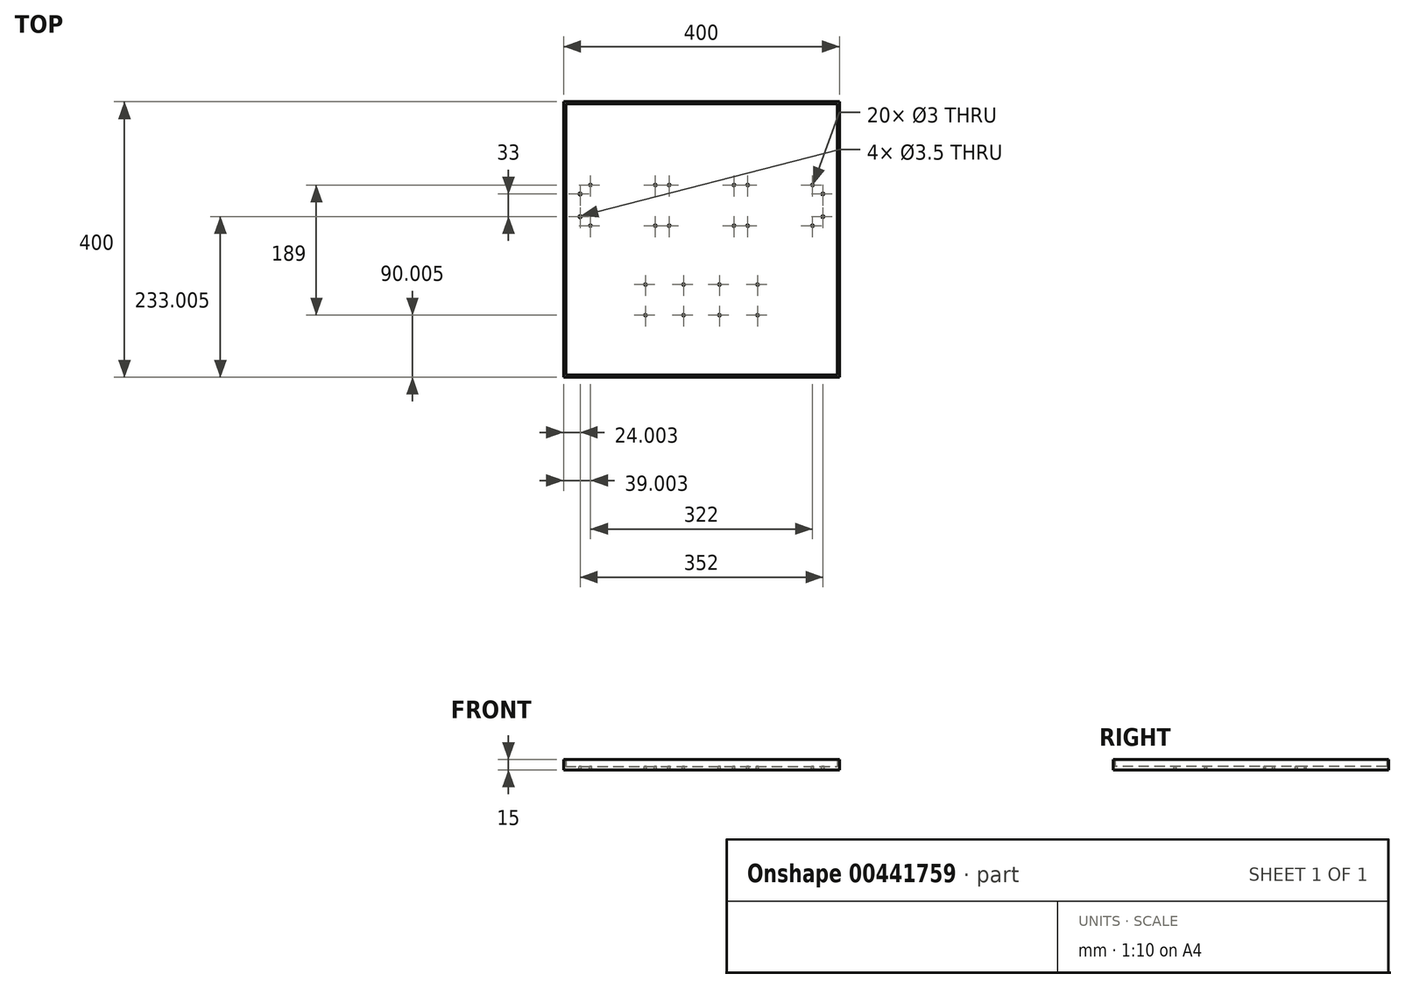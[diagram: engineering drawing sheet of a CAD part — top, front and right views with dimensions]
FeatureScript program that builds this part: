
annotation { "Feature Type Name" : "Feature", "Feature Type Description" : "" }
export const myFeature = defineFeature(function(context is Context, id is Id, definition is map)
    precondition{}
    {
        {
            var Q0;
            Q0=qCreatedBy(makeId("Top.planeOp"),FACE);
            var sketch = newSketch(context, id + "F0", { "sketchPlane" : qUnion([Q0])});
            skLineSegment(sketch, "E0.bottom", {"start": v(-197.38, 325.18) * mm, "end": v(202.62, 325.18) * mm});
            skLineSegment(sketch, "E0.top", {"start": v(-197.38, -74.82) * mm, "end": v(202.62, -74.82) * mm});
            skLineSegment(sketch, "E0.left", {"start": v(-197.38, 325.18) * mm, "end": v(-197.38, -74.82) * mm});
            skLineSegment(sketch, "E0.right", {"start": v(202.62, 325.18) * mm, "end": v(202.62, -74.82) * mm});
            skSolve(sketch);
        }
        {
            var Q0;
            Q0=qSketchRegion(id+"F0",true);
            extrude(context, id + "F1", {"entities" : qUnion([Q0]), "depth" : 5 * mm});
        }
        {
            var Q0;
            Q0=makeQuery(id+"F1.opExtrude","CAP_FACE",FACE,{"disambiguationData":[OSD([sQuery(id+"F0.wireOp",EDGE,"E0.bottom"),sQuery(id+"F0.wireOp",EDGE,"E0.top"),sQuery(id+"F0.wireOp",EDGE,"E0.left"),sQuery(id+"F0.wireOp",EDGE,"E0.right")])],"isStart":false});
            var sketch = newSketch(context, id + "F2", { "sketchPlane" : qUnion([Q0])});
            skCircle(sketch, "E1", {"center": v(-158.38, 145.18) * mm, "radius": 1.5 * mm});
            skCircle(sketch, "E2", {"center": v(-64.38, 145.18) * mm, "radius": 1.5 * mm});
            skCircle(sketch, "E3", {"center": v(-44.38, 145.18) * mm, "radius": 1.5 * mm});
            skCircle(sketch, "E4", {"center": v(49.62, 145.18) * mm, "radius": 1.5 * mm});
            skCircle(sketch, "E5", {"center": v(69.62, 145.18) * mm, "radius": 1.5 * mm});
            skCircle(sketch, "E6", {"center": v(163.62, 145.18) * mm, "radius": 1.5 * mm});
            skCircle(sketch, "E7.0.1.0", {"center": v(-44.38, 204.18) * mm, "radius": 1.5 * mm});
            skCircle(sketch, "E7.0.1.1", {"center": v(-158.38, 204.18) * mm, "radius": 1.5 * mm});
            skCircle(sketch, "E7.0.1.2", {"center": v(49.62, 204.18) * mm, "radius": 1.5 * mm});
            skCircle(sketch, "E7.0.1.3", {"center": v(69.62, 204.18) * mm, "radius": 1.5 * mm});
            skCircle(sketch, "E7.0.1.4", {"center": v(163.62, 204.18) * mm, "radius": 1.5 * mm});
            skCircle(sketch, "E7.0.1.5", {"center": v(-64.38, 204.18) * mm, "radius": 1.5 * mm});
            skLineSegment(sketch, "E7.direction1", {"start": v(-158.38, 145.18) * mm, "end": v(-133.38, 145.18) * mm, "construction": true});
            skLineSegment(sketch, "E7.direction2", {"start": v(-158.38, 145.18) * mm, "end": v(-158.38, 204.18) * mm, "construction": true});
            skCircle(sketch, "E8", {"center": v(-173.38, 158.18) * mm, "radius": 1.75 * mm});
            skCircle(sketch, "E9.0.1.0", {"center": v(-173.38, 191.18) * mm, "radius": 1.75 * mm});
            skLineSegment(sketch, "E9.direction1", {"start": v(-173.38, 158.18) * mm, "end": v(178.62, 158.18) * mm, "construction": true});
            skLineSegment(sketch, "E9.direction2", {"start": v(-173.38, 158.18) * mm, "end": v(-173.38, 191.18) * mm, "construction": true});
            skCircle(sketch, "E10.0.1.0", {"center": v(178.62, 158.18) * mm, "radius": 1.75 * mm});
            skCircle(sketch, "E10.0.1.1", {"center": v(178.62, 191.18) * mm, "radius": 1.75 * mm});
            skSolve(sketch);
        }
        {
            var Q0;
            Q0=qSketchRegion(id+"F2",true);
            extrude(context, id + "F3", {"entities" : qUnion([Q0]), "operationType" : NewBodyOperationType.REMOVE, "endBound" : BoundingType.THROUGH_ALL, "oppositeDirection" : true, "depth" : 25 * mm});
        }
        {
            var Q0;
            Q0=makeQuery(id+"F1.opExtrude","CAP_FACE",FACE,{"disambiguationData":[OSD([sQuery(id+"F0.wireOp",EDGE,"E0.bottom"),sQuery(id+"F0.wireOp",EDGE,"E0.top"),sQuery(id+"F0.wireOp",EDGE,"E0.left"),sQuery(id+"F0.wireOp",EDGE,"E0.right")])],"isStart":false});
            var sketch = newSketch(context, id + "F4", { "sketchPlane" : qUnion([Q0])});
            skCircle(sketch, "E11", {"center": v(-23.38, 15.18) * mm, "radius": 1.5 * mm});
            skCircle(sketch, "E12.0.1.0", {"center": v(-23.38, 59.63) * mm, "radius": 1.5 * mm});
            skCircle(sketch, "E12.1.0.0", {"center": v(28.62, 15.18) * mm, "radius": 1.5 * mm});
            skCircle(sketch, "E12.1.1.0", {"center": v(28.62, 59.63) * mm, "radius": 1.5 * mm});
            skLineSegment(sketch, "E12.direction1", {"start": v(-23.38, 15.18) * mm, "end": v(28.62, 15.18) * mm, "construction": true});
            skLineSegment(sketch, "E12.direction2", {"start": v(-23.38, 15.18) * mm, "end": v(-23.38, 59.63) * mm, "construction": true});
            skSolve(sketch);
        }
        {
            var Q0;
            Q0=qSketchRegion(id+"F4",true);
            extrude(context, id + "F5", {"entities" : qUnion([Q0]), "operationType" : NewBodyOperationType.REMOVE, "endBound" : BoundingType.THROUGH_ALL, "oppositeDirection" : true, "depth" : 25 * mm});
        }
        {
            var Q0;
            Q0=makeQuery(id+"F1.opExtrude","CAP_FACE",FACE,{"disambiguationData":[OSD([sQuery(id+"F0.wireOp",EDGE,"E0.bottom"),sQuery(id+"F0.wireOp",EDGE,"E0.top"),sQuery(id+"F0.wireOp",EDGE,"E0.left"),sQuery(id+"F0.wireOp",EDGE,"E0.right")])],"isStart":false});
            var sketch = newSketch(context, id + "F6", { "sketchPlane" : qUnion([Q0])});
            skCircle(sketch, "E13", {"center": v(-78.65, 15.18) * mm, "radius": 1.5 * mm});
            skCircle(sketch, "E14.0.1.0", {"center": v(-78.65, 59.63) * mm, "radius": 1.5 * mm});
            skCircle(sketch, "E14.1.0.0", {"center": v(83.9, 15.18) * mm, "radius": 1.5 * mm});
            skCircle(sketch, "E14.1.1.0", {"center": v(83.9, 59.63) * mm, "radius": 1.5 * mm});
            skLineSegment(sketch, "E14.direction1", {"start": v(-78.65, 15.18) * mm, "end": v(83.9, 15.18) * mm, "construction": true});
            skLineSegment(sketch, "E14.direction2", {"start": v(-78.65, 15.18) * mm, "end": v(-78.65, 59.63) * mm, "construction": true});
            skSolve(sketch);
        }
        {
            var Q0;
            Q0=qSketchRegion(id+"F6",true);
            extrude(context, id + "F7", {"entities" : qUnion([Q0]), "operationType" : NewBodyOperationType.REMOVE, "endBound" : BoundingType.THROUGH_ALL, "oppositeDirection" : true, "depth" : 25 * mm});
        }
        {
            assignVariable(context, id + "F8", {"name" : "H", "anyValue" : 10});
        }
        {
            var Q0;
            Q0=makeQuery(id+"F1.opExtrude","CAP_FACE",FACE,{"disambiguationData":[OSD([sQuery(id+"F0.wireOp",EDGE,"E0.bottom"),sQuery(id+"F0.wireOp",EDGE,"E0.top"),sQuery(id+"F0.wireOp",EDGE,"E0.left"),sQuery(id+"F0.wireOp",EDGE,"E0.right")])],"isStart":false});
            var sketch = newSketch(context, id + "F9", { "sketchPlane" : qUnion([Q0])});
            skLineSegment(sketch, "E15.bottom", {"start": v(-197.38, -74.82) * mm, "end": v(202.62, -74.82) * mm});
            skLineSegment(sketch, "E15.top", {"start": v(-197.38, -71.82) * mm, "end": v(202.62, -71.82) * mm});
            skLineSegment(sketch, "E15.left", {"start": v(-197.38, -74.82) * mm, "end": v(-197.38, -71.82) * mm});
            skLineSegment(sketch, "E15.right", {"start": v(202.62, -74.82) * mm, "end": v(202.62, -71.82) * mm});
            skLineSegment(sketch, "E16.bottom", {"start": v(-197.38, -71.82) * mm, "end": v(-194.38, -71.82) * mm});
            skLineSegment(sketch, "E16.top", {"start": v(-197.38, 325.18) * mm, "end": v(-194.38, 325.18) * mm});
            skLineSegment(sketch, "E16.left", {"start": v(-197.38, -71.82) * mm, "end": v(-197.38, 325.18) * mm});
            skLineSegment(sketch, "E16.right", {"start": v(-194.38, -71.82) * mm, "end": v(-194.38, 325.18) * mm});
            skLineSegment(sketch, "E17.bottom", {"start": v(-194.38, 325.18) * mm, "end": v(202.62, 325.18) * mm});
            skLineSegment(sketch, "E17.top", {"start": v(-194.38, 322.18) * mm, "end": v(202.62, 322.18) * mm});
            skLineSegment(sketch, "E17.left", {"start": v(-194.38, 325.18) * mm, "end": v(-194.38, 322.18) * mm});
            skLineSegment(sketch, "E17.right", {"start": v(202.62, 325.18) * mm, "end": v(202.62, 322.18) * mm});
            skLineSegment(sketch, "E18.bottom", {"start": v(202.62, 322.18) * mm, "end": v(199.62, 322.18) * mm});
            skLineSegment(sketch, "E18.top", {"start": v(202.62, -71.82) * mm, "end": v(199.62, -71.82) * mm});
            skLineSegment(sketch, "E18.left", {"start": v(202.62, 322.18) * mm, "end": v(202.62, -71.82) * mm});
            skLineSegment(sketch, "E18.right", {"start": v(199.62, 322.18) * mm, "end": v(199.62, -71.82) * mm});
            skSolve(sketch);
        }
        {
            var Q0;
            Q0 = qSketchRegion(id + "F9", true);
            extrude(context, id + "F10", {"entities" : qUnion([Q0]), "operationType" : NewBodyOperationType.ADD, "depth" : (getVariable(context, 'H')) * mm});
        }
        {
            var Q0;
            Q0=makeQuery(id+"F10.boolean.opBoolean","MERGE",FACE,{"derivedFrom":[makeQuery(id+"F1.opExtrude","SWEPT_FACE",FACE,{"disambiguationData":[OSD([sQuery(id+"F0.wireOp",EDGE,"E0.top")])]}),makeQuery(id+"F10.opExtrude","SWEPT_FACE",FACE,{"disambiguationData":[OSD([sQuery(id+"F9.wireOp",EDGE,"E15.bottom")])]})]});
            var sketch = newSketch(context, id + "F11", { "sketchPlane" : qUnion([Q0])});
            skLineSegment(sketch, "E19.bottom", {"start": v(15, 15) * mm, "end": v(-15, 15) * mm});
            skLineSegment(sketch, "E19.top", {"start": v(15, 30) * mm, "end": v(-15, 30) * mm});
            skLineSegment(sketch, "E19.left", {"start": v(15, 30) * mm, "end": v(15, 15) * mm});
            skLineSegment(sketch, "E19.right", {"start": v(-15, 30) * mm, "end": v(-15, 15) * mm});
            skPoint(sketch, "E19.middle", {"position": v(0, 22.5) * mm});
            skSolve(sketch);
        }
        {
            var Q0;
            Q0 = qSketchRegion(id + "F11", true);
            var Q1;
            Q1=makeQuery(id+"F10.opExtrude","SWEPT_FACE",FACE,{"disambiguationData":[OSD([sQuery(id+"F9.wireOp",EDGE,"E15.top")])]});
            extrude(context, id + "F12", {"entities" : qUnion([Q0]), "operationType" : NewBodyOperationType.REMOVE, "endBound" : BoundingType.UP_TO_SURFACE, "oppositeDirection" : true, "endBoundEntityFace" : qUnion([Q1]), "depth" : 25 * mm});
        }
        {
            var Q0;
            Q0=makeQuery(id+"F10.boolean.opBoolean","MERGE",FACE,{"derivedFrom":[makeQuery(id+"F1.opExtrude","SWEPT_FACE",FACE,{"disambiguationData":[OSD([sQuery(id+"F0.wireOp",EDGE,"E0.bottom")])]}),makeQuery(id+"F10.opExtrude","SWEPT_FACE",FACE,{"disambiguationData":[OSD([sQuery(id+"F9.wireOp",EDGE,"E16.top"),sQuery(id+"F9.wireOp",EDGE,"E17.bottom")])]})]});
            var sketch = newSketch(context, id + "F13", { "sketchPlane" : qUnion([Q0])});
            skLineSegment(sketch, "E20.bottom", {"start": v(15, 15) * mm, "end": v(-15, 15) * mm});
            skLineSegment(sketch, "E20.top", {"start": v(15, 30) * mm, "end": v(-15, 30) * mm});
            skLineSegment(sketch, "E20.left", {"start": v(15, 30) * mm, "end": v(15, 15) * mm});
            skLineSegment(sketch, "E20.right", {"start": v(-15, 30) * mm, "end": v(-15, 15) * mm});
            skPoint(sketch, "E20.middle", {"position": v(0, 22.5) * mm});
            skSolve(sketch);
        }
        {
            var Q0;
            Q0 = qSketchRegion(id + "F13", true);
            var Q1;
            Q1=makeQuery(id+"F10.opExtrude","SWEPT_FACE",FACE,{"disambiguationData":[OSD([sQuery(id+"F9.wireOp",EDGE,"E17.top")])]});
            extrude(context, id + "F14", {"entities" : qUnion([Q0]), "operationType" : NewBodyOperationType.REMOVE, "endBound" : BoundingType.UP_TO_SURFACE, "oppositeDirection" : true, "endBoundEntityFace" : qUnion([Q1]), "depth" : 25 * mm});
        }
    });
